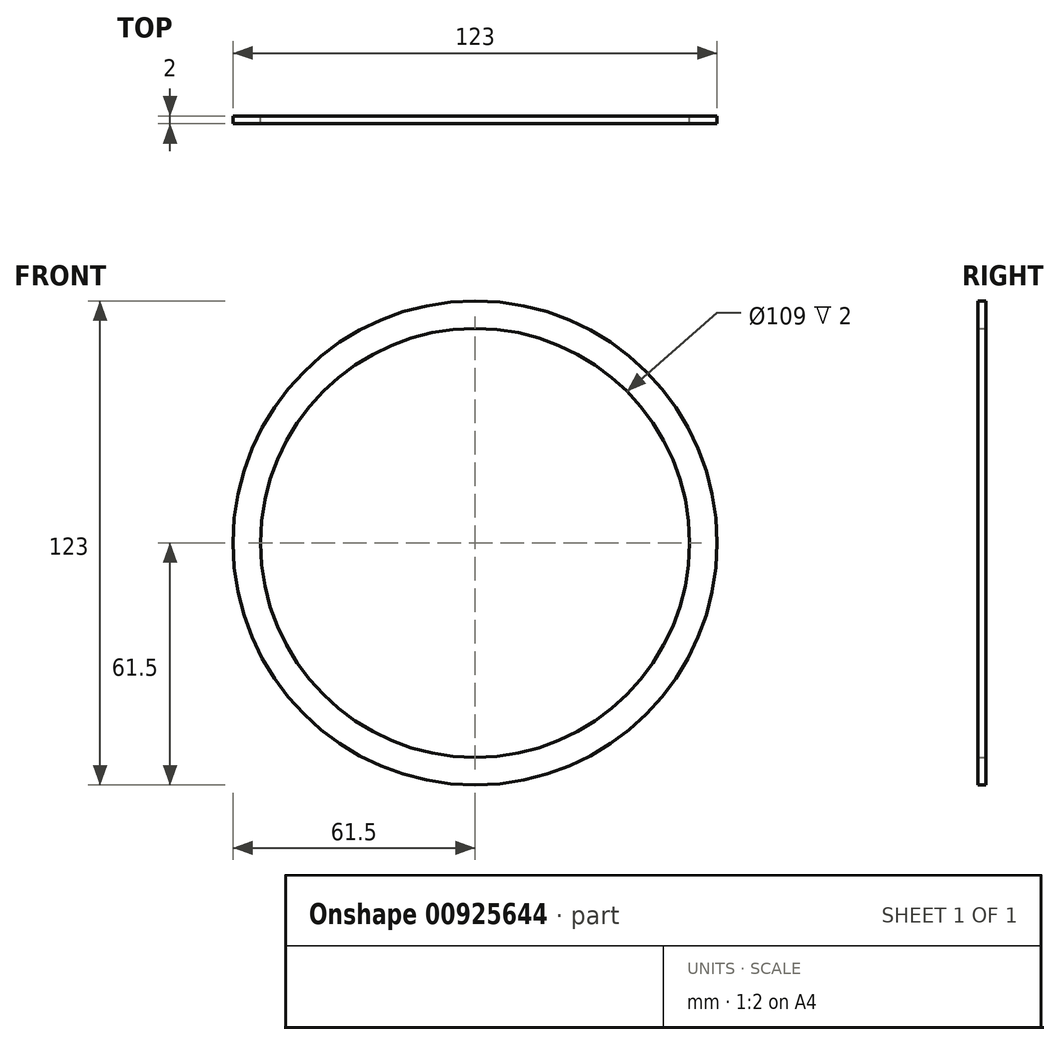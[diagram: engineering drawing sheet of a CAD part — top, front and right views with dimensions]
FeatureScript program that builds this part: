
annotation { "Feature Type Name" : "Feature", "Feature Type Description" : "" }
export const myFeature = defineFeature(function(context is Context, id is Id, definition is map)
    precondition{}
    {
        {
            var Q0;
            Q0=qCreatedBy(makeId("Front.planeOp"),FACE);
            var sketch = newSketch(context, id + "F0", { "sketchPlane" : qUnion([Q0])});
            skCircle(sketch, "E0", {"center": v(0, 0) * mm, "radius": 61.5 * mm});
            skCircle(sketch, "E1", {"center": v(0, 0) * mm, "radius": 54.5 * mm});
            skSolve(sketch);
        }
        {
            var Q0;
            Q0=makeQuery(id+"F0.imprint","IMPRINT",FACE,{"disambiguationData":[TD([[makeQuery(id+"F0.imprint","IMPRINT",EDGE,{"derivedFrom":sQuery(id+"F0.wireOp",EDGE,"E0")}),1.0]])]});
            extrude(context, id + "F1", {"entities" : qUnion([Q0]), "depth" : 2 * mm, "offsetDistance" : 25 * mm});
        }
    });
